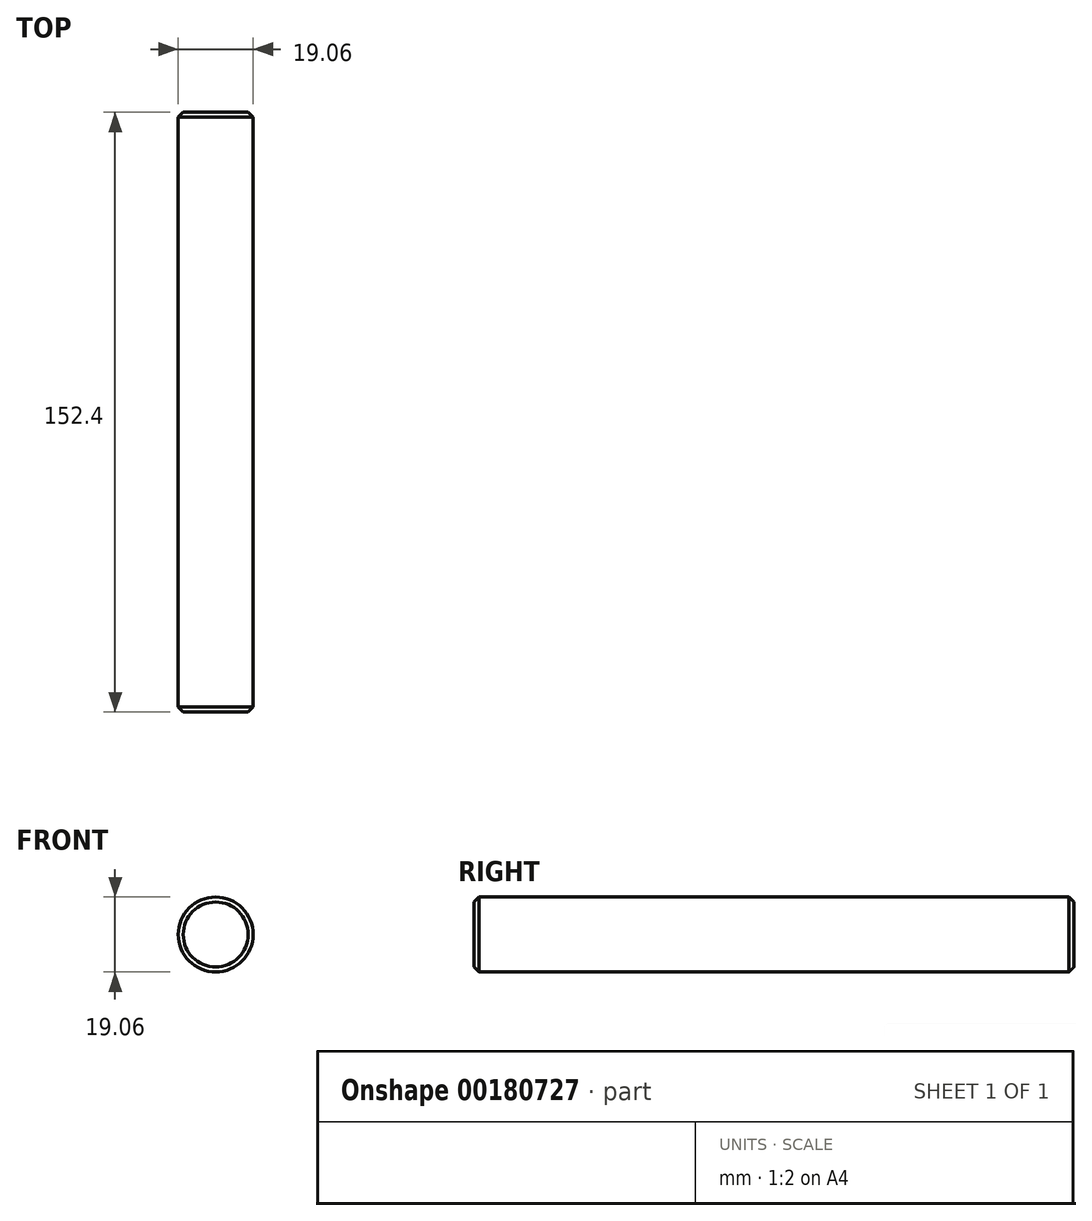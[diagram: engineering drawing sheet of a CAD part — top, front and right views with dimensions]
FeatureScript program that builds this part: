
annotation { "Feature Type Name" : "Feature", "Feature Type Description" : "" }
export const myFeature = defineFeature(function(context is Context, id is Id, definition is map)
    precondition{}
    {
        {
            var Q0;
            Q0=qCreatedBy(makeId("Front.planeOp"),FACE);
            var sketch = newSketch(context, id + "F0", { "sketchPlane" : qUnion([Q0])});
            skCircle(sketch, "E0", {"center": v(0, 0) * mm, "radius": 9.53 * mm});
            skSolve(sketch);
        }
        {
            var Q0;
            Q0=makeQuery(id+"F0.imprint","IMPRINT",FACE,{"disambiguationData":[TD([[makeQuery(id+"F0.imprint","IMPRINT",EDGE,{"derivedFrom":sQuery(id+"F0.wireOp",EDGE,"E0")}),1.0]])]});
            extrude(context, id + "F1", {"entities" : qUnion([Q0]), "depth" : 152.4 * mm});
        }
        {
            var Q0;
            Q0=makeQuery(id+"F1.opExtrude","CAP_EDGE",EDGE,{"disambiguationData":[OSD([sQuery(id+"F0.wireOp",EDGE,"E0")])],"isStart":true});
            chamfer(context, id + "F2", {"entities" : qUnion([Q0]), "chamferType" : ChamferType.OFFSET_ANGLE, "width" : 1.27 * mm, "oppositeDirection" : false, "angle" : 45 * degree, "tangentPropagation" : true});
        }
        {
            var Q0;
            Q0=makeQuery(id+"F1.opExtrude","CAP_EDGE",EDGE,{"disambiguationData":[OSD([sQuery(id+"F0.wireOp",EDGE,"E0")])],"isStart":false});
            chamfer(context, id + "F3", {"entities" : qUnion([Q0]), "chamferType" : ChamferType.OFFSET_ANGLE, "width" : 1.27 * mm, "oppositeDirection" : false, "angle" : 45 * degree, "tangentPropagation" : true});
        }
    });
